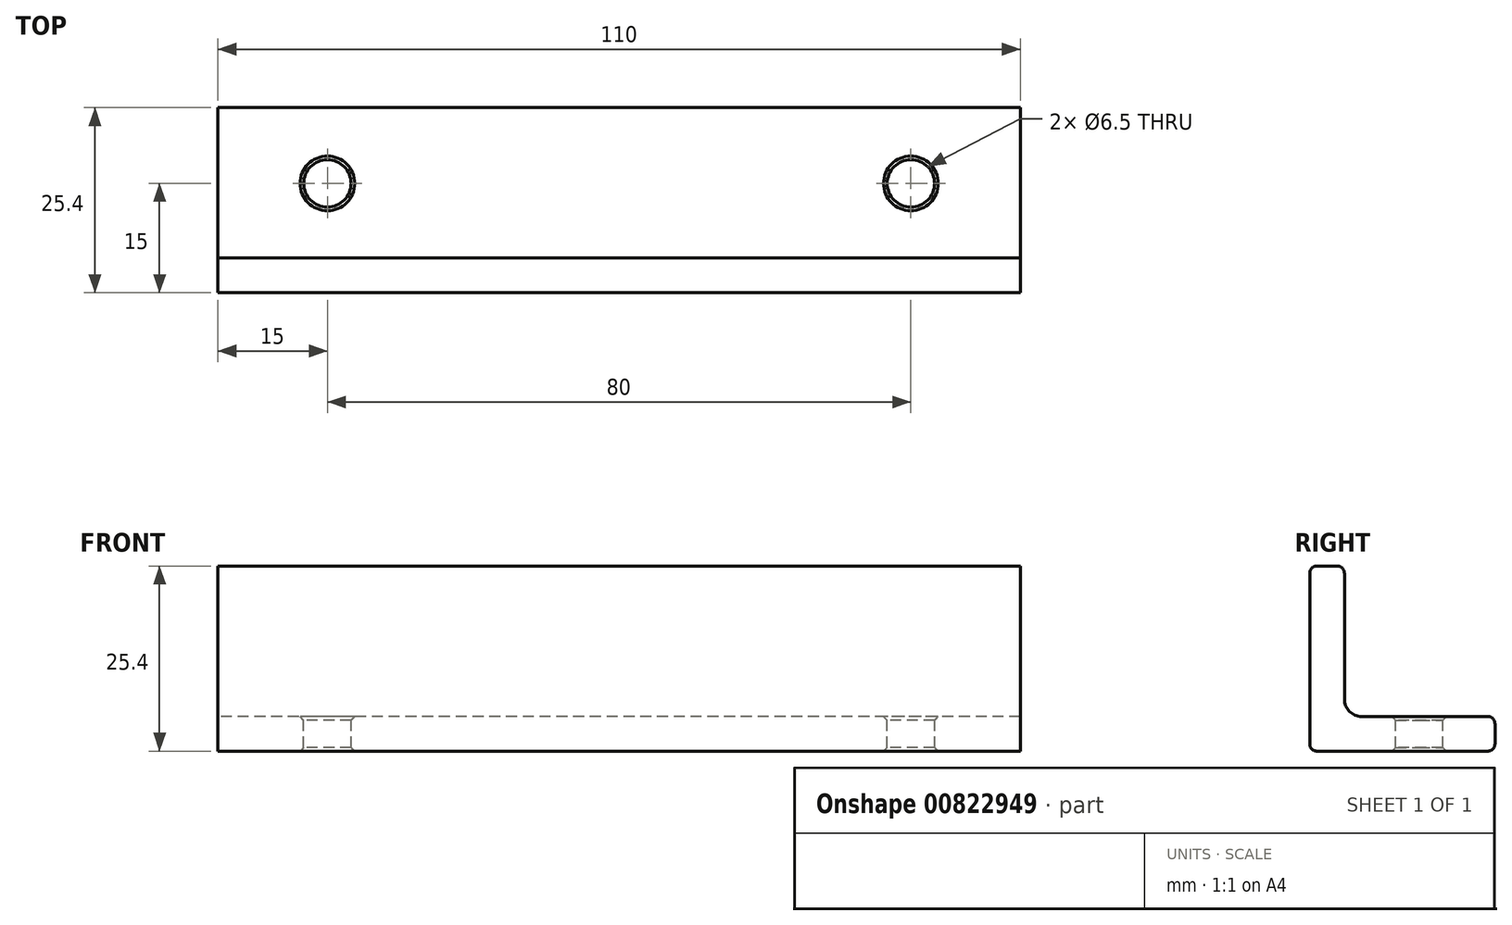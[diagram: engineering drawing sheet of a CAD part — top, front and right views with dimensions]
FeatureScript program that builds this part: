
annotation { "Feature Type Name" : "Feature", "Feature Type Description" : "" }
export const myFeature = defineFeature(function(context is Context, id is Id, definition is map)
    precondition{}
    {
        {
            var Q0;
            Q0=qCreatedBy(makeId("Right.planeOp"),FACE);
            var sketch = newSketch(context, id + "F0", { "sketchPlane" : qUnion([Q0])});
            skLineSegment(sketch, "E0", {"start": v(0, 0) * mm, "end": v(25.4, 0) * mm});
            skLineSegment(sketch, "E1", {"start": v(0, 0) * mm, "end": v(0, 25.4) * mm});
            skLineSegment(sketch, "E2", {"start": v(0, 25.4) * mm, "end": v(4.76, 25.4) * mm});
            skLineSegment(sketch, "E3", {"start": v(4.76, 25.4) * mm, "end": v(4.76, 4.76) * mm});
            skLineSegment(sketch, "E4", {"start": v(4.76, 4.76) * mm, "end": v(25.4, 4.76) * mm});
            skLineSegment(sketch, "E5", {"start": v(25.4, 4.76) * mm, "end": v(25.4, 0) * mm});
            skSolve(sketch);
        }
        {
            var Q0;
            Q0=qSketchRegion(id+"F0",true);
            extrude(context, id + "F1", {"entities" : qUnion([Q0]), "endBound" : BoundingType.SYMMETRIC, "depth" : 110 * mm, "offsetDistance" : 25 * mm});
        }
        {
            var Q0;
            Q0=makeQuery(id+"F1.opExtrude","SWEPT_EDGE",EDGE,{"disambiguationData":[OSD([sQuery(id+"F0.wireOp",EDGE,"E1"),sQuery(id+"F0.wireOp",EDGE,"E2")])]});
            var Q1;
            Q1=makeQuery(id+"F1.opExtrude","SWEPT_EDGE",EDGE,{"disambiguationData":[OSD([sQuery(id+"F0.wireOp",EDGE,"E2"),sQuery(id+"F0.wireOp",EDGE,"E3")])]});
            var Q2;
            Q2=makeQuery(id+"F1.opExtrude","SWEPT_EDGE",EDGE,{"disambiguationData":[OSD([sQuery(id+"F0.wireOp",EDGE,"E0"),sQuery(id+"F0.wireOp",EDGE,"E1")])]});
            var Q3;
            Q3=makeQuery(id+"F1.opExtrude","SWEPT_EDGE",EDGE,{"disambiguationData":[OSD([sQuery(id+"F0.wireOp",EDGE,"E4"),sQuery(id+"F0.wireOp",EDGE,"E5")])]});
            var Q4;
            Q4=makeQuery(id+"F1.opExtrude","SWEPT_EDGE",EDGE,{"disambiguationData":[OSD([sQuery(id+"F0.wireOp",EDGE,"E0"),sQuery(id+"F0.wireOp",EDGE,"E5")])]});
            fillet(context, id + "F2", {"entities" : qUnion([Q0, Q1, Q2, Q3, Q4]), "radius" : 1 * mm, "tangentPropagation" : true, "allowEdgeOverflow" : false});
        }
        {
            var Q0;
            Q0=makeQuery(id+"F1.opExtrude","SWEPT_EDGE",EDGE,{"disambiguationData":[OSD([sQuery(id+"F0.wireOp",EDGE,"E3"),sQuery(id+"F0.wireOp",EDGE,"E4")])]});
            fillet(context, id + "F3", {"entities" : qUnion([Q0]), "radius" : (3 * 25.4 / 16 / 2) * mm, "tangentPropagation" : true, "allowEdgeOverflow" : false});
        }
        {
            var Q0;
            Q0=makeQuery(id+"F1.opExtrude","SWEPT_FACE",FACE,{"disambiguationData":[OSD([sQuery(id+"F0.wireOp",EDGE,"E4")])]});
            var sketch = newSketch(context, id + "F4", { "sketchPlane" : qUnion([Q0])});
            skLineSegment(sketch, "E6.0", {"start": v(-55, 0) * mm, "end": v(55, 0) * mm, "construction": true});
            skLineSegment(sketch, "E7.0", {"start": v(-55, 1) * mm, "end": v(-55, 24.4) * mm, "construction": true});
            skCircle(sketch, "E8", {"center": v(-40, 15) * mm, "radius": 3.25 * mm});
            skLineSegment(sketch, "E9.0", {"start": v(-55, 25.4) * mm, "end": v(55, 25.4) * mm, "construction": true});
            skCircle(sketch, "E10.1.0.0", {"center": v(325, 15) * mm, "radius": 3.25 * mm, "construction": true});
            skCircle(sketch, "E10.2.0.0", {"center": v(690, 15) * mm, "radius": 3.25 * mm});
            skCircle(sketch, "E10.3.0.0", {"center": v(1055, 15) * mm, "radius": 3.25 * mm, "construction": true});
            skCircle(sketch, "E10.4.0.0", {"center": v(1420, 15) * mm, "radius": 3.25 * mm});
            skLineSegment(sketch, "E10.direction1", {"start": v(-40, 15) * mm, "end": v(-20, 15) * mm, "construction": true});
            skLineSegment(sketch, "E11", {"start": v(0, 0) * mm, "end": v(0, -29.98) * mm, "construction": true});
            skCircle(sketch, "E12.MirrorC", {"center": v(40, 15) * mm, "radius": 3.25 * mm});
            skSolve(sketch);
        }
        {
            var Q0;
            Q0=qSketchRegion(id+"F4",true);
            extrude(context, id + "F5", {"entities" : qUnion([Q0]), "operationType" : NewBodyOperationType.REMOVE, "oppositeDirection" : true, "depth" : 25 * mm, "offsetDistance" : 25 * mm});
        }
        {
            var Q0;
            Q0=makeQuery(id+"F5.boolean.opBoolean","COPY",FACE,{"derivedFrom":makeQuery(id+"F5.opExtrude","SWEPT_FACE",FACE,{"disambiguationData":[OSD([sQuery(id+"F4.wireOp",EDGE,"E8")])]})});
            var Q1;
            Q1=makeQuery(id+"F5.boolean.opBoolean","COPY",FACE,{"derivedFrom":makeQuery(id+"F5.opExtrude","SWEPT_FACE",FACE,{"disambiguationData":[OSD([sQuery(id+"F4.wireOp",EDGE,"E10.1.0.0")])]})});
            var Q2;
            Q2=makeQuery(id+"F5.boolean.opBoolean","COPY",FACE,{"derivedFrom":makeQuery(id+"F5.opExtrude","SWEPT_FACE",FACE,{"disambiguationData":[OSD([sQuery(id+"F4.wireOp",EDGE,"E10.2.0.0")])]})});
            var Q3;
            Q3=makeQuery(id+"F5.boolean.opBoolean","COPY",FACE,{"derivedFrom":makeQuery(id+"F5.opExtrude","SWEPT_FACE",FACE,{"disambiguationData":[OSD([sQuery(id+"F4.wireOp",EDGE,"E10.3.0.0")])]})});
            var Q4;
            Q4=makeQuery(id+"F5.boolean.opBoolean","COPY",FACE,{"derivedFrom":makeQuery(id+"F5.opExtrude","SWEPT_FACE",FACE,{"disambiguationData":[OSD([sQuery(id+"F4.wireOp",EDGE,"E10.4.0.0")])]})});
            var Q5;
            Q5=makeQuery(id+"F5.boolean.opBoolean","COPY",FACE,{"derivedFrom":makeQuery(id+"F5.opExtrude","SWEPT_FACE",FACE,{"disambiguationData":[OSD([sQuery(id+"F4.wireOp",EDGE,"E12.MirrorC")])]})});
            chamfer(context, id + "F6", {"entities" : qUnion([Q0, Q1, Q2, Q3, Q4, Q5]), "width" : 0.5 * mm, "tangentPropagation" : true});
        }
    });
